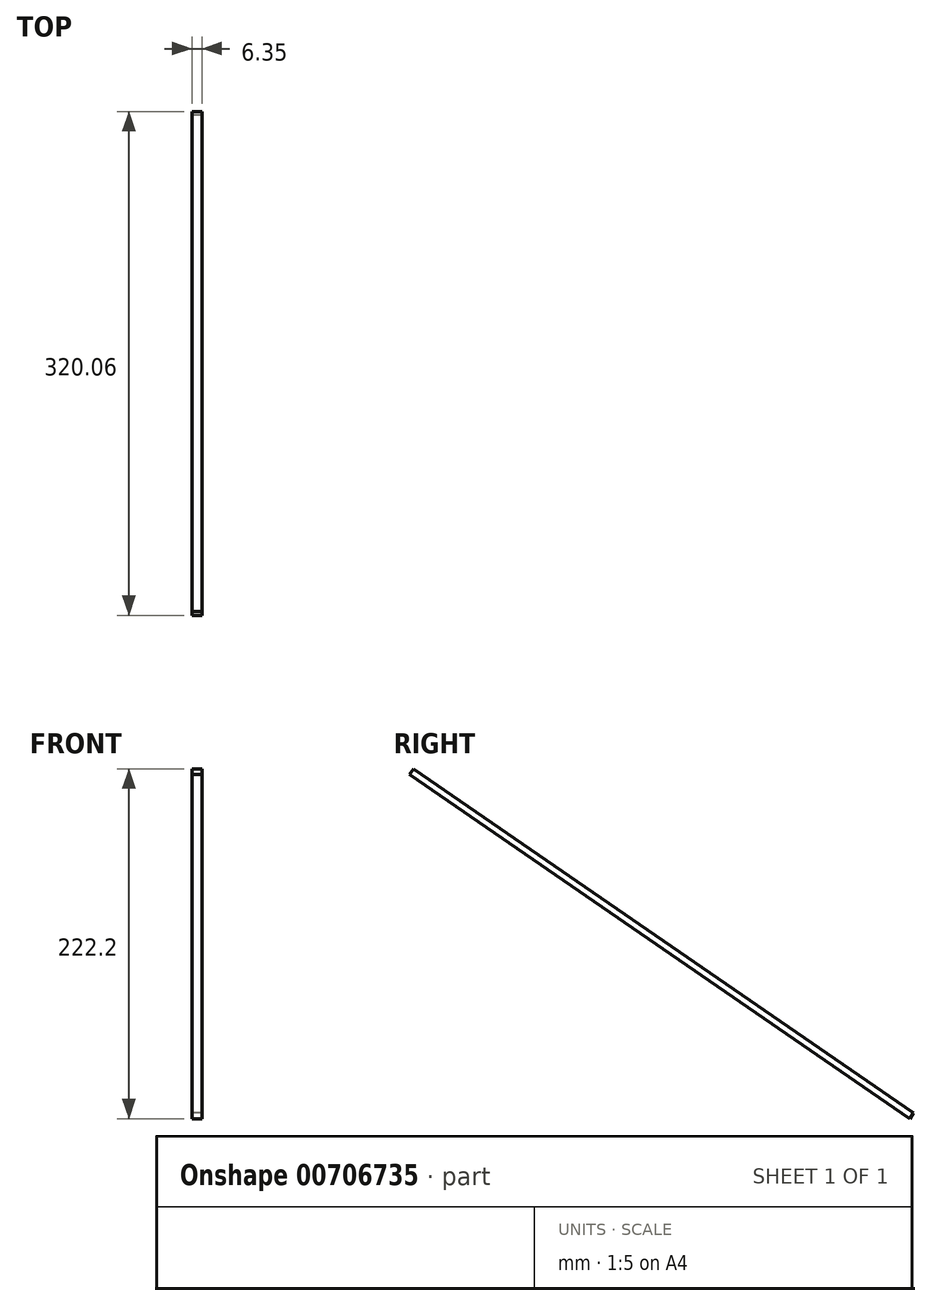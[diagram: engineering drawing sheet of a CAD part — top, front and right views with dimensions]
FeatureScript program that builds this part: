
annotation { "Feature Type Name" : "Feature", "Feature Type Description" : "" }
export const myFeature = defineFeature(function(context is Context, id is Id, definition is map)
    precondition{}
    {
        {
            var Q0;
            Q0=qCreatedBy(makeId("Right.planeOp"),FACE);
            var sketch = newSketch(context, id + "F0", { "sketchPlane" : qUnion([Q0])});
            skLineSegment(sketch, "E0", {"start": v(0, 0) * mm, "end": v(-114.08, 78.53) * mm});
            skLineSegment(sketch, "E1", {"start": v(-114.08, 78.53) * mm, "end": v(-116.49, 75.04) * mm});
            skLineSegment(sketch, "E2", {"start": v(-116.49, 75.04) * mm, "end": v(-2.34, -3.54) * mm});
            skLineSegment(sketch, "E3", {"start": v(-2.34, -3.54) * mm, "end": v(0, 0) * mm});
            skSolve(sketch);
        }
        {
            var Q0;
            Q0=qSketchRegion(id+"F0",true);
            extrude(context, id + "F1", {"entities" : qUnion([Q0]), "depth" : 6.35 * mm, "offsetDistance" : 25.4 * mm});
        }
        {
            var Q0;
            Q0=makeQuery(id+"F1.opExtrude","SWEPT_FACE",FACE,{"disambiguationData":[OSD([sQuery(id+"F0.wireOp",EDGE,"E1")])]});
            extrude(context, id + "F2", {"entities" : qUnion([Q0]), "operationType" : NewBodyOperationType.ADD, "depth" : 247.14 * mm, "offsetDistance" : 25.4 * mm});
        }
    });
